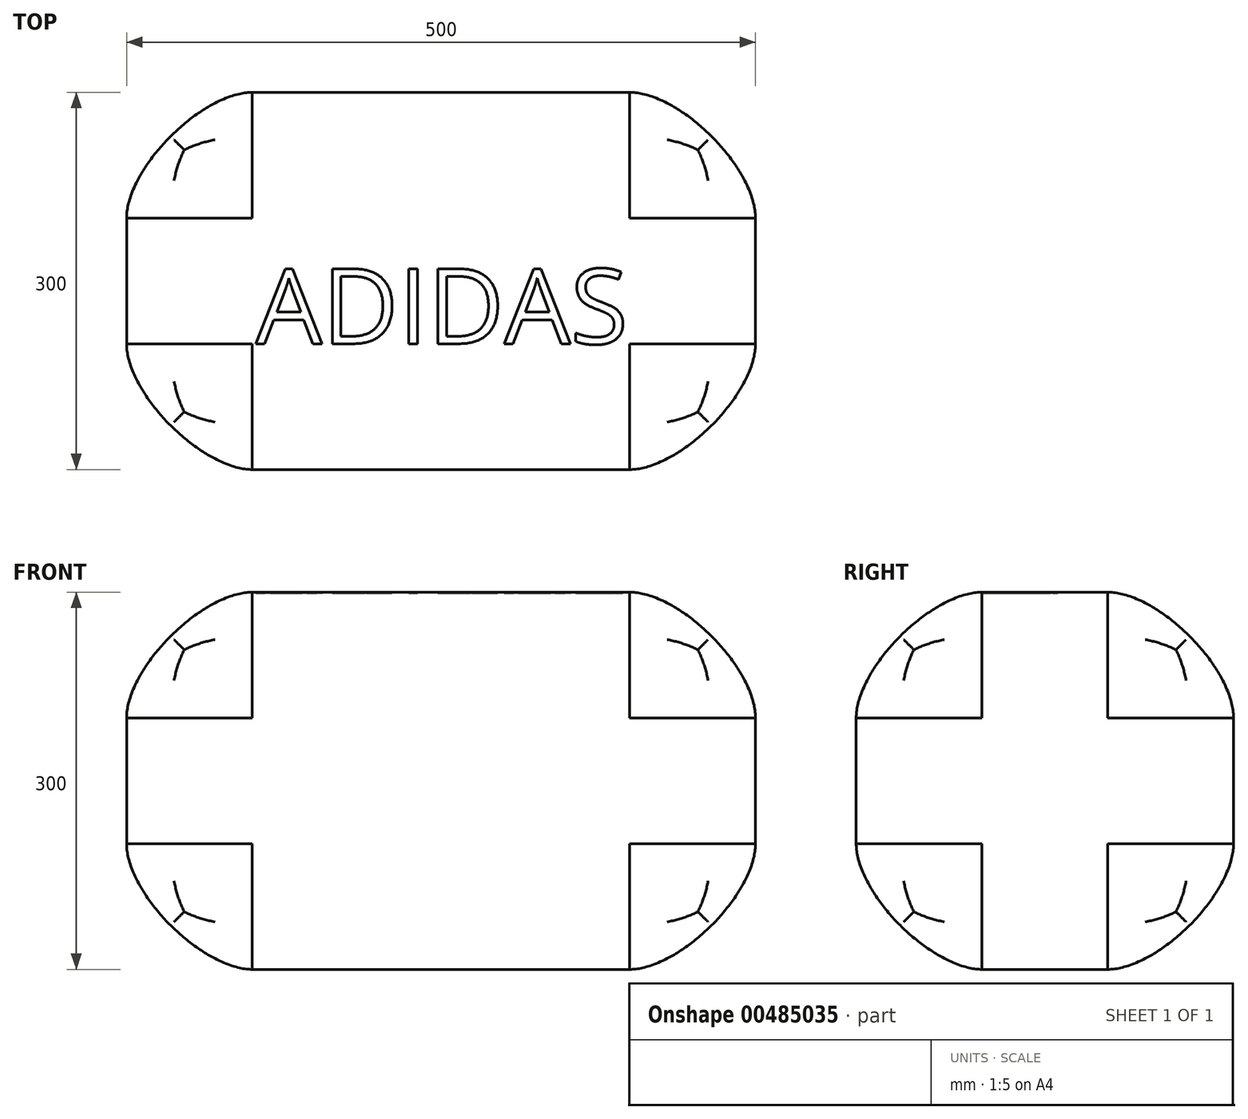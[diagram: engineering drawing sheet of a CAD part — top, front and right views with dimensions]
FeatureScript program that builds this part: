
annotation { "Feature Type Name" : "Feature", "Feature Type Description" : "" }
export const myFeature = defineFeature(function(context is Context, id is Id, definition is map)
    precondition{}
    {
        {
            var Q0;
            Q0=qCreatedBy(makeId("Top.planeOp"),FACE);
            var sketch = newSketch(context, id + "F0", { "sketchPlane" : qUnion([Q0])});
            skLineSegment(sketch, "E0.bottom", {"start": v(250, 150) * mm, "end": v(-250, 150) * mm});
            skLineSegment(sketch, "E0.top", {"start": v(250, -150) * mm, "end": v(-250, -150) * mm});
            skLineSegment(sketch, "E0.left", {"start": v(250, 150) * mm, "end": v(250, -150) * mm});
            skLineSegment(sketch, "E0.right", {"start": v(-250, 150) * mm, "end": v(-250, -150) * mm});
            skPoint(sketch, "E0.middle", {"position": v(0, 0) * mm});
            skSolve(sketch);
        }
        {
            var Q0;
            Q0 = qSketchRegion(id + "F0", true);
            extrude(context, id + "F1", {"entities" : qUnion([Q0]), "depth" : 300 * mm});
        }
        {
            var Q0;
            Q0=makeQuery(id+"F1.opExtrude","SWEPT_FACE",FACE,{"disambiguationData":[OSD([sQuery(id+"F0.wireOp",EDGE,"E0.top")])]});
            var Q1;
            Q1=makeQuery(id+"F1.opExtrude","SWEPT_EDGE",EDGE,{"disambiguationData":[OSD([sQuery(id+"F0.wireOp",EDGE,"E0.top"),sQuery(id+"F0.wireOp",EDGE,"E0.right")])]});
            var Q2;
            Q2=makeQuery(id+"F1.opExtrude","CAP_FACE",FACE,{"disambiguationData":[OSD([sQuery(id+"F0.wireOp",EDGE,"E0.bottom"),sQuery(id+"F0.wireOp",EDGE,"E0.top"),sQuery(id+"F0.wireOp",EDGE,"E0.left"),sQuery(id+"F0.wireOp",EDGE,"E0.right")])],"isStart":false});
            var Q3;
            Q3=makeQuery(id+"F1.opExtrude","SWEPT_EDGE",EDGE,{"disambiguationData":[OSD([sQuery(id+"F0.wireOp",EDGE,"E0.top"),sQuery(id+"F0.wireOp",EDGE,"E0.left")])]});
            var Q4;
            Q4=makeQuery(id+"F1.opExtrude","CAP_FACE",FACE,{"disambiguationData":[OSD([sQuery(id+"F0.wireOp",EDGE,"E0.bottom"),sQuery(id+"F0.wireOp",EDGE,"E0.top"),sQuery(id+"F0.wireOp",EDGE,"E0.left"),sQuery(id+"F0.wireOp",EDGE,"E0.right")])],"isStart":true});
            var Q5;
            Q5=makeQuery(id+"F1.opExtrude","SWEPT_FACE",FACE,{"disambiguationData":[OSD([sQuery(id+"F0.wireOp",EDGE,"E0.bottom")])]});
            var Q6;
            Q6=makeQuery(id+"F1.opExtrude","SWEPT_EDGE",EDGE,{"disambiguationData":[OSD([sQuery(id+"F0.wireOp",EDGE,"E0.bottom"),sQuery(id+"F0.wireOp",EDGE,"E0.left")])]});
            var Q7;
            Q7=makeQuery(id+"F1.opExtrude","SWEPT_FACE",FACE,{"disambiguationData":[OSD([sQuery(id+"F0.wireOp",EDGE,"E0.left")])]});
            var Q8;
            Q8=makeQuery(id+"F1.opExtrude","CAP_EDGE",EDGE,{"disambiguationData":[OSD([sQuery(id+"F0.wireOp",EDGE,"E0.bottom")])],"isStart":false});
            var Q9;
            Q9=makeQuery(id+"F1.opExtrude","SWEPT_FACE",FACE,{"disambiguationData":[OSD([sQuery(id+"F0.wireOp",EDGE,"E0.right")])]});
            var Q10;
            Q10=makeQuery(id+"F1.opExtrude","CAP_EDGE",EDGE,{"disambiguationData":[OSD([sQuery(id+"F0.wireOp",EDGE,"E0.top")])],"isStart":true});
            var Q11;
            Q11=makeQuery(id+"F1.opExtrude","CAP_EDGE",EDGE,{"disambiguationData":[OSD([sQuery(id+"F0.wireOp",EDGE,"E0.top")])],"isStart":false});
            var Q12;
            Q12=makeQuery(id+"F1.opExtrude","CAP_EDGE",EDGE,{"disambiguationData":[OSD([sQuery(id+"F0.wireOp",EDGE,"E0.left")])],"isStart":true});
            var Q13;
            Q13=makeQuery(id+"F1.opExtrude","CAP_EDGE",EDGE,{"disambiguationData":[OSD([sQuery(id+"F0.wireOp",EDGE,"E0.left")])],"isStart":false});
            var Q14;
            Q14=makeQuery(id+"F1.opExtrude","CAP_EDGE",EDGE,{"disambiguationData":[OSD([sQuery(id+"F0.wireOp",EDGE,"E0.right")])],"isStart":false});
            var Q15;
            Q15=makeQuery(id+"F1.opExtrude","SWEPT_EDGE",EDGE,{"disambiguationData":[OSD([sQuery(id+"F0.wireOp",EDGE,"E0.bottom"),sQuery(id+"F0.wireOp",EDGE,"E0.right")])]});
            var Q16;
            Q16=makeQuery(id+"F1.opExtrude","CAP_EDGE",EDGE,{"disambiguationData":[OSD([sQuery(id+"F0.wireOp",EDGE,"E0.bottom")])],"isStart":true});
            var Q17;
            Q17=makeQuery(id+"F1.opExtrude","CAP_EDGE",EDGE,{"disambiguationData":[OSD([sQuery(id+"F0.wireOp",EDGE,"E0.right")])],"isStart":true});
            fillet(context, id + "F2", {"entities" : qUnion([Q0, Q1, Q2, Q3, Q4, Q5, Q6, Q7, Q8, Q9, Q10, Q11, Q12, Q13, Q14, Q15, Q16, Q17]), "radius" : 100 * mm, "tangentPropagation" : true, "rho" : 0.3, "crossSection" : FilletCrossSection.CONIC, "allowEdgeOverflow" : false});
        }
        {
            var Q0;
            Q0=makeQuery(id+"F1.opExtrude","CAP_FACE",FACE,{"disambiguationData":[OSD([sQuery(id+"F0.wireOp",EDGE,"E0.bottom"),sQuery(id+"F0.wireOp",EDGE,"E0.top"),sQuery(id+"F0.wireOp",EDGE,"E0.left"),sQuery(id+"F0.wireOp",EDGE,"E0.right")])],"isStart":false});
            var sketch = newSketch(context, id + "F3", { "sketchPlane" : qUnion([Q0])});
            skText(sketch, "E1", { "text": "ADIDAS", "fontName": "OpenSans-Regular.ttf"});
            const initialGuessF3  = {"E1": [-0.14736, -0.05, 1, 0, 0.06]};
            skSetInitialGuess(sketch, initialGuessF3);
            skSolve(sketch);
        }
        {
            var Q0;
            Q0 = qSketchRegion(id + "F3", true);
            extrude(context, id + "F4", {"entities" : qUnion([Q0]), "operationType" : NewBodyOperationType.REMOVE, "oppositeDirection" : true, "depth" : 1 * mm});
        }
    });
